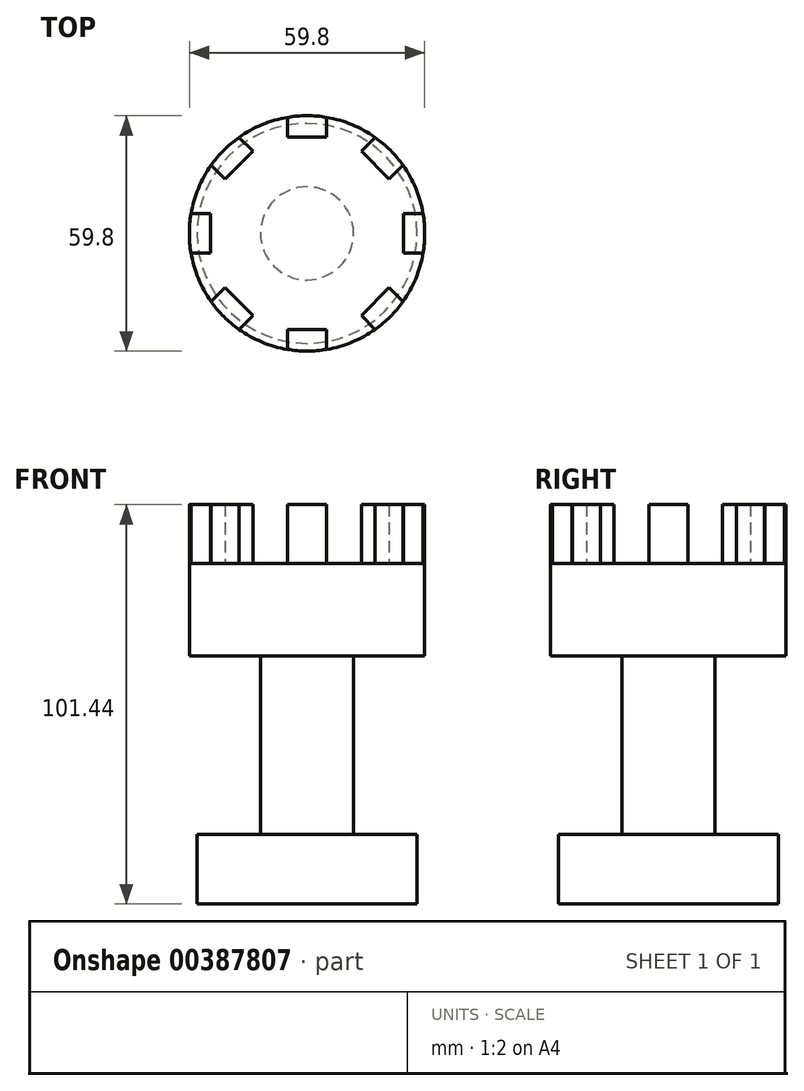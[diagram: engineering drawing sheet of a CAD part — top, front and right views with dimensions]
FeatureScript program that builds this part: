
annotation { "Feature Type Name" : "Feature", "Feature Type Description" : "" }
export const myFeature = defineFeature(function(context is Context, id is Id, definition is map)
    precondition{}
    {
        {
            var Q0;
            Q0=qCreatedBy(makeId("Front.planeOp"),FACE);
            var sketch = newSketch(context, id + "F0", { "sketchPlane" : qUnion([Q0])});
            skLineSegment(sketch, "E0", {"start": v(0, 105.68) * mm, "end": v(0, -136.23) * mm, "construction": true});
            skLineSegment(sketch, "E1", {"start": v(0, 47.51) * mm, "end": v(0, -38.93) * mm});
            skLineSegment(sketch, "E2", {"start": v(0, -38.93) * mm, "end": v(27.94, -38.93) * mm});
            skLineSegment(sketch, "E3", {"start": v(27.94, -38.93) * mm, "end": v(27.94, -21.35) * mm});
            skLineSegment(sketch, "E4", {"start": v(27.94, -21.35) * mm, "end": v(11.83, -21.35) * mm});
            skLineSegment(sketch, "E5", {"start": v(11.83, -21.35) * mm, "end": v(11.83, 24.07) * mm});
            skLineSegment(sketch, "E6", {"start": v(11.83, 24.07) * mm, "end": v(29.9, 24.07) * mm});
            skLineSegment(sketch, "E7", {"start": v(29.9, 24.07) * mm, "end": v(29.9, 45.07) * mm});
            skLineSegment(sketch, "E8", {"start": v(0, 47.51) * mm, "end": v(29.9, 47.51) * mm});
            skLineSegment(sketch, "E9", {"start": v(29.9, 47.51) * mm, "end": v(29.9, 45.07) * mm});
            skSolve(sketch);
        }
        {
            var Q0;
            Q0 = qSketchRegion(id + "F0", true);
            var Q1;
            Q1=sQuery(id+"F0.wireOp",EDGE,"E0");
            revolve(context, id + "F1", {"entities" : qUnion([Q0]), "axis" : qUnion([Q1]), "revolveType" : RevolveType.FULL});
        }
        {
            var Q0;
            Q0=makeQuery(id+"F1.opRevolve","SWEPT_FACE",FACE,{"disambiguationData":[OSD([sQuery(id+"F0.wireOp",EDGE,"E8")])]});
            var sketch = newSketch(context, id + "F2", { "sketchPlane" : qUnion([Q0])});
            skLineSegment(sketch, "E10", {"start": v(-5, 29.48) * mm, "end": v(-5, 24.48) * mm});
            skLineSegment(sketch, "E11", {"start": v(-5, 24.48) * mm, "end": v(5, 24.48) * mm});
            skLineSegment(sketch, "E12", {"start": v(5, 24.48) * mm, "end": v(5, 29.48) * mm});
            skArc(sketch, "E13", {"start": v(5, 29.48) * mm, "mid": v(0, 29.9) * mm, "end": v(-5, 29.48) * mm});
            skSolve(sketch);
        }
        {
            var Q0;
            Q0 = qSketchRegion(id + "F2", true);
            extrude(context, id + "F3", {"entities" : qUnion([Q0]), "operationType" : NewBodyOperationType.ADD, "depth" : 15 * mm});
        }
        {
            var Q0;
            Q0=makeQuery(id+"F1.opRevolve","SWEPT_BODY",BODY,{"disambiguationData":[OSD([sQuery(id+"F0.wireOp",EDGE,"E1"),sQuery(id+"F0.wireOp",EDGE,"E2"),sQuery(id+"F0.wireOp",EDGE,"E3"),sQuery(id+"F0.wireOp",EDGE,"E4"),sQuery(id+"F0.wireOp",EDGE,"E5"),sQuery(id+"F0.wireOp",EDGE,"E6"),sQuery(id+"F0.wireOp",EDGE,"E7"),sQuery(id+"F0.wireOp",EDGE,"E8"),sQuery(id+"F0.wireOp",EDGE,"E9")])]});
            var Q1;
            Q1=makeQuery(id+"F3.boolean.opBoolean","MERGE",FACE,{"derivedFrom":[makeQuery(id+"F1.opRevolve","SWEPT_FACE",FACE,{"disambiguationData":[OSD([sQuery(id+"F0.wireOp",EDGE,"E7"),sQuery(id+"F0.wireOp",EDGE,"E9")])]}),makeQuery(id+"F3.opExtrude","SWEPT_FACE",FACE,{"disambiguationData":[OSD([sQuery(id+"F2.wireOp",EDGE,"E13")])]})]});
            circularPattern(context, id + "F4", {"entities" : qUnion([Q0]), "axis" : qUnion([Q1]), "angle" : 360 * degree, "instanceCount" : 8, "equalSpace" : true});
        }
    });
